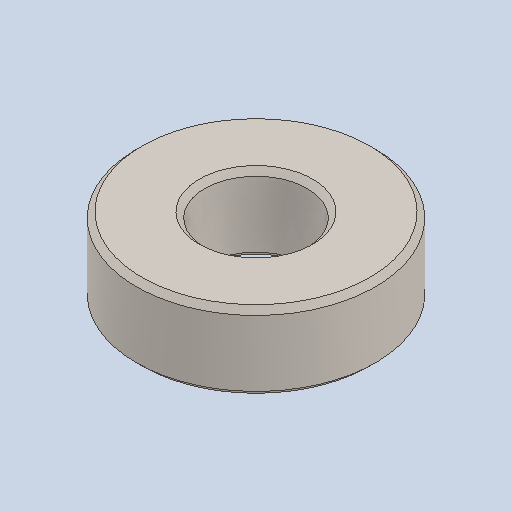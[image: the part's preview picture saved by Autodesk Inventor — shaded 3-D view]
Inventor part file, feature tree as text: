
AUTODESK INVENTOR PART (.ipt)
format: ipt  version: 2024.2 (Build 282272000, 272)  size: 105,472 bytes
history: native  units: in
note: dims shown in document units (in); Inventor stores cm internally (conversion verified against a paired STEP export)
features: chamfer x1
ambient origin geometry x8: Origin, YZ Plane, XZ Plane, XY Plane, X Axis, Y Axis, Z Axis, Center Point
bodies: Solid1 (feature_tree)
feature tree (1):
  chamfer  "Chamfer1"  [1 undecoded]
note: 1 required parameter value undecoded (feature->parameter linkage not recoverable at this tier; creation-order binding heuristic only, values carry confidence <= 0.55)
